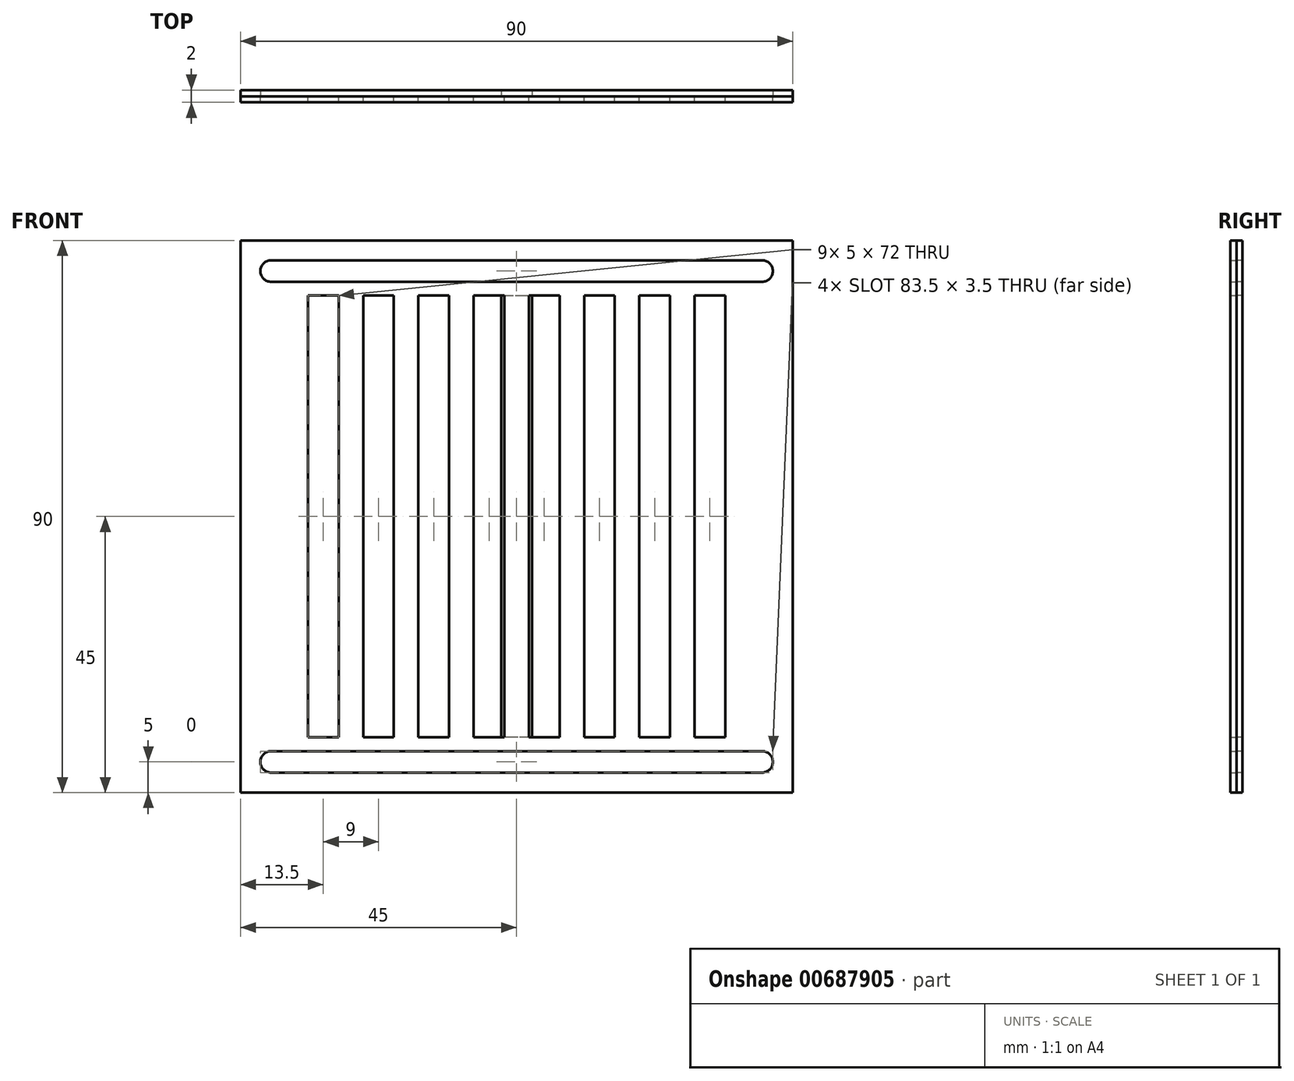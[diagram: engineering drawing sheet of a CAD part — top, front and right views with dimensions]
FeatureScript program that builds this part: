
annotation { "Feature Type Name" : "Feature", "Feature Type Description" : "" }
export const myFeature = defineFeature(function(context is Context, id is Id, definition is map)
    precondition{}
    {
        {
            var Q0;
            Q0=qCreatedBy(makeId("Front.planeOp"),FACE);
            var sketch = newSketch(context, id + "F0", { "sketchPlane" : qUnion([Q0])});
            skLineSegment(sketch, "E0.bottom", {"start": v(-45, 45) * mm, "end": v(45, 45) * mm});
            skLineSegment(sketch, "E0.top", {"start": v(-45, -45) * mm, "end": v(45, -45) * mm});
            skLineSegment(sketch, "E0.left", {"start": v(-45, 45) * mm, "end": v(-45, -45) * mm});
            skLineSegment(sketch, "E0.right", {"start": v(45, 45) * mm, "end": v(45, -45) * mm});
            skPoint(sketch, "E0.middle", {"position": v(0, 0) * mm});
            skLineSegment(sketch, "E1", {"start": v(0, 41.75) * mm, "end": v(40, 41.75) * mm});
            skLineSegment(sketch, "E2", {"start": v(0, 38.25) * mm, "end": v(40, 38.25) * mm});
            skArc(sketch, "E3", {"start": v(40, 41.75) * mm, "mid": v(41.75, 40) * mm, "end": v(40, 38.25) * mm});
            skLineSegment(sketch, "E4.top", {"start": v(2, 36) * mm, "end": v(7, 36) * mm});
            skLineSegment(sketch, "E4.left", {"start": v(2, 0) * mm, "end": v(2, 36) * mm});
            skLineSegment(sketch, "E4.right", {"start": v(7, 0) * mm, "end": v(7, 36) * mm});
            skLineSegment(sketch, "E5.1.0.0", {"start": v(11, 0) * mm, "end": v(11, 36) * mm});
            skLineSegment(sketch, "E5.1.0.1", {"start": v(11, 36) * mm, "end": v(16, 36) * mm});
            skLineSegment(sketch, "E5.1.0.2", {"start": v(16, 0) * mm, "end": v(16, 36) * mm});
            skLineSegment(sketch, "E5.2.0.0", {"start": v(20, 0) * mm, "end": v(20, 36) * mm});
            skLineSegment(sketch, "E5.2.0.1", {"start": v(20, 36) * mm, "end": v(25, 36) * mm});
            skLineSegment(sketch, "E5.2.0.2", {"start": v(25, 0) * mm, "end": v(25, 36) * mm});
            skLineSegment(sketch, "E5.3.0.0", {"start": v(29, 0) * mm, "end": v(29, 36) * mm});
            skLineSegment(sketch, "E5.3.0.1", {"start": v(29, 36) * mm, "end": v(34, 36) * mm});
            skLineSegment(sketch, "E5.3.0.2", {"start": v(34, 0) * mm, "end": v(34, 36) * mm});
            skLineSegment(sketch, "E5.direction1", {"start": v(2, 0) * mm, "end": v(12, 0) * mm, "construction": true});
            skLineSegment(sketch, "E6.MirrorCS", {"start": v(-25, 0) * mm, "end": v(-25, 36) * mm});
            skLineSegment(sketch, "E7.MirrorCS", {"start": v(-20, 36) * mm, "end": v(-25, 36) * mm});
            skLineSegment(sketch, "E8.MirrorCS", {"start": v(-20, 0) * mm, "end": v(-20, 36) * mm});
            skLineSegment(sketch, "E9.MirrorCS", {"start": v(-2, 0) * mm, "end": v(-12, 0) * mm, "construction": true});
            skLineSegment(sketch, "E10.MirrorCS", {"start": v(-29, 36) * mm, "end": v(-34, 36) * mm});
            skLineSegment(sketch, "E11.MirrorCS", {"start": v(-29, 0) * mm, "end": v(-29, 36) * mm});
            skLineSegment(sketch, "E12.MirrorCS", {"start": v(-16, 0) * mm, "end": v(-16, 36) * mm});
            skLineSegment(sketch, "E13.MirrorCS", {"start": v(-11, 36) * mm, "end": v(-16, 36) * mm});
            skLineSegment(sketch, "E14.MirrorCS", {"start": v(-34, 0) * mm, "end": v(-34, 36) * mm});
            skLineSegment(sketch, "E15.MirrorCS", {"start": v(0, 41.75) * mm, "end": v(-40, 41.75) * mm});
            skLineSegment(sketch, "E16.MirrorCS", {"start": v(-2, 36) * mm, "end": v(-7, 36) * mm});
            skLineSegment(sketch, "E17.MirrorCS", {"start": v(-2, 0) * mm, "end": v(-2, 36) * mm});
            skArc(sketch, "E18.MirrorCS", {"start": v(-40, 41.75) * mm, "mid": v(-41.75, 40) * mm, "end": v(-40, 38.25) * mm});
            skLineSegment(sketch, "E19.MirrorCS", {"start": v(-7, 0) * mm, "end": v(-7, 36) * mm});
            skLineSegment(sketch, "E20.MirrorCS", {"start": v(-11, 0) * mm, "end": v(-11, 36) * mm});
            skLineSegment(sketch, "E21.MirrorCS", {"start": v(0, 38.25) * mm, "end": v(-40, 38.25) * mm});
            skArc(sketch, "E22.MirrorCS", {"start": v(40, -41.75) * mm, "mid": v(41.75, -40) * mm, "end": v(40, -38.25) * mm});
            skArc(sketch, "E23.MirrorCS", {"start": v(-40, -41.75) * mm, "mid": v(-41.75, -40) * mm, "end": v(-40, -38.25) * mm});
            skLineSegment(sketch, "E24.MirrorCS", {"start": v(-7, 0) * mm, "end": v(-7, -36) * mm});
            skLineSegment(sketch, "E25.MirrorCS", {"start": v(25, 0) * mm, "end": v(25, -36) * mm});
            skLineSegment(sketch, "E26.MirrorCS", {"start": v(29, 0) * mm, "end": v(29, -36) * mm});
            skLineSegment(sketch, "E27.MirrorCS", {"start": v(-11, 0) * mm, "end": v(-11, -36) * mm});
            skLineSegment(sketch, "E28.MirrorCS", {"start": v(34, 0) * mm, "end": v(34, -36) * mm});
            skLineSegment(sketch, "E29.MirrorCS", {"start": v(0, -41.75) * mm, "end": v(-40, -41.75) * mm});
            skLineSegment(sketch, "E30.MirrorCS", {"start": v(-25, 0) * mm, "end": v(-25, -36) * mm});
            skLineSegment(sketch, "E31.MirrorCS", {"start": v(-2, 0) * mm, "end": v(-2, -36) * mm});
            skLineSegment(sketch, "E32.MirrorCS", {"start": v(-20, 0) * mm, "end": v(-20, -36) * mm});
            skLineSegment(sketch, "E33.MirrorCS", {"start": v(-29, 0) * mm, "end": v(-29, -36) * mm});
            skLineSegment(sketch, "E34.MirrorCS", {"start": v(-11, -36) * mm, "end": v(-16, -36) * mm});
            skLineSegment(sketch, "E35.MirrorCS", {"start": v(16, 0) * mm, "end": v(16, -36) * mm});
            skLineSegment(sketch, "E36.MirrorCS", {"start": v(11, -36) * mm, "end": v(16, -36) * mm});
            skLineSegment(sketch, "E37.MirrorCS", {"start": v(11, 0) * mm, "end": v(11, -36) * mm});
            skLineSegment(sketch, "E38.MirrorCS", {"start": v(7, 0) * mm, "end": v(7, -36) * mm});
            skLineSegment(sketch, "E39.MirrorCS", {"start": v(2, 0) * mm, "end": v(2, -36) * mm});
            skLineSegment(sketch, "E40.MirrorCS", {"start": v(2, -36) * mm, "end": v(7, -36) * mm});
            skLineSegment(sketch, "E41.MirrorCS", {"start": v(20, -36) * mm, "end": v(25, -36) * mm});
            skLineSegment(sketch, "E42.MirrorCS", {"start": v(29, -36) * mm, "end": v(34, -36) * mm});
            skLineSegment(sketch, "E43.MirrorCS", {"start": v(20, 0) * mm, "end": v(20, -36) * mm});
            skLineSegment(sketch, "E44.MirrorCS", {"start": v(0, -38.25) * mm, "end": v(-40, -38.25) * mm});
            skLineSegment(sketch, "E45.MirrorCS", {"start": v(-34, 0) * mm, "end": v(-34, -36) * mm});
            skLineSegment(sketch, "E46.MirrorCS", {"start": v(-16, 0) * mm, "end": v(-16, -36) * mm});
            skLineSegment(sketch, "E47.MirrorCS", {"start": v(-29, -36) * mm, "end": v(-34, -36) * mm});
            skLineSegment(sketch, "E48.MirrorCS", {"start": v(-20, -36) * mm, "end": v(-25, -36) * mm});
            skLineSegment(sketch, "E49.MirrorCS", {"start": v(-2, -36) * mm, "end": v(-7, -36) * mm});
            skLineSegment(sketch, "E50.MirrorCS", {"start": v(0, -41.75) * mm, "end": v(40, -41.75) * mm});
            skLineSegment(sketch, "E51.MirrorCS", {"start": v(0, -38.25) * mm, "end": v(40, -38.25) * mm});
            skSolve(sketch);
        }
        {
            var Q0;
            Q0=makeQuery(id+"F0.imprint","IMPRINT",FACE,{"disambiguationData":[TD([[makeQuery(id+"F0.imprint","IMPRINT",EDGE,{"derivedFrom":sQuery(id+"F0.wireOp",EDGE,"E0.bottom")}),-1.0]])]});
            extrude(context, id + "F1", {"entities" : qUnion([Q0]), "depth" : 1 * mm, "offsetDistance" : 25 * mm});
        }
        {
            var Q0;
            Q0=makeQuery(id+"F1.opExtrude","CAP_FACE",FACE,{"disambiguationData":[OSD([sQuery(id+"F0.wireOp",EDGE,"E0.bottom"),sQuery(id+"F0.wireOp",EDGE,"E0.top"),sQuery(id+"F0.wireOp",EDGE,"E0.left"),sQuery(id+"F0.wireOp",EDGE,"E0.right"),sQuery(id+"F0.wireOp",EDGE,"E1"),sQuery(id+"F0.wireOp",EDGE,"E2"),sQuery(id+"F0.wireOp",EDGE,"E3"),sQuery(id+"F0.wireOp",EDGE,"E4.top"),sQuery(id+"F0.wireOp",EDGE,"E4.left"),sQuery(id+"F0.wireOp",EDGE,"E4.right"),sQuery(id+"F0.wireOp",EDGE,"E5.1.0.0"),sQuery(id+"F0.wireOp",EDGE,"E5.1.0.1"),sQuery(id+"F0.wireOp",EDGE,"E5.1.0.2"),sQuery(id+"F0.wireOp",EDGE,"E5.2.0.0"),sQuery(id+"F0.wireOp",EDGE,"E5.2.0.1"),sQuery(id+"F0.wireOp",EDGE,"E5.2.0.2"),sQuery(id+"F0.wireOp",EDGE,"E5.3.0.0"),sQuery(id+"F0.wireOp",EDGE,"E5.3.0.1"),sQuery(id+"F0.wireOp",EDGE,"E5.3.0.2"),sQuery(id+"F0.wireOp",EDGE,"E6.MirrorCS"),sQuery(id+"F0.wireOp",EDGE,"E7.MirrorCS"),sQuery(id+"F0.wireOp",EDGE,"E8.MirrorCS"),sQuery(id+"F0.wireOp",EDGE,"E10.MirrorCS"),sQuery(id+"F0.wireOp",EDGE,"E11.MirrorCS"),sQuery(id+"F0.wireOp",EDGE,"E12.MirrorCS"),sQuery(id+"F0.wireOp",EDGE,"E13.MirrorCS"),sQuery(id+"F0.wireOp",EDGE,"E14.MirrorCS"),sQuery(id+"F0.wireOp",EDGE,"E15.MirrorCS"),sQuery(id+"F0.wireOp",EDGE,"E16.MirrorCS"),sQuery(id+"F0.wireOp",EDGE,"E17.MirrorCS"),sQuery(id+"F0.wireOp",EDGE,"E18.MirrorCS"),sQuery(id+"F0.wireOp",EDGE,"E19.MirrorCS"),sQuery(id+"F0.wireOp",EDGE,"E20.MirrorCS"),sQuery(id+"F0.wireOp",EDGE,"E21.MirrorCS"),sQuery(id+"F0.wireOp",EDGE,"E22.MirrorCS"),sQuery(id+"F0.wireOp",EDGE,"E23.MirrorCS"),sQuery(id+"F0.wireOp",EDGE,"E24.MirrorCS"),sQuery(id+"F0.wireOp",EDGE,"E25.MirrorCS"),sQuery(id+"F0.wireOp",EDGE,"E26.MirrorCS"),sQuery(id+"F0.wireOp",EDGE,"E27.MirrorCS"),sQuery(id+"F0.wireOp",EDGE,"E28.MirrorCS"),sQuery(id+"F0.wireOp",EDGE,"E29.MirrorCS"),sQuery(id+"F0.wireOp",EDGE,"E30.MirrorCS"),sQuery(id+"F0.wireOp",EDGE,"E31.MirrorCS"),sQuery(id+"F0.wireOp",EDGE,"E32.MirrorCS"),sQuery(id+"F0.wireOp",EDGE,"E33.MirrorCS"),sQuery(id+"F0.wireOp",EDGE,"E34.MirrorCS"),sQuery(id+"F0.wireOp",EDGE,"E35.MirrorCS"),sQuery(id+"F0.wireOp",EDGE,"E36.MirrorCS"),sQuery(id+"F0.wireOp",EDGE,"E37.MirrorCS"),sQuery(id+"F0.wireOp",EDGE,"E38.MirrorCS"),sQuery(id+"F0.wireOp",EDGE,"E39.MirrorCS"),sQuery(id+"F0.wireOp",EDGE,"E40.MirrorCS"),sQuery(id+"F0.wireOp",EDGE,"E41.MirrorCS"),sQuery(id+"F0.wireOp",EDGE,"E42.MirrorCS"),sQuery(id+"F0.wireOp",EDGE,"E43.MirrorCS"),sQuery(id+"F0.wireOp",EDGE,"E44.MirrorCS"),sQuery(id+"F0.wireOp",EDGE,"E45.MirrorCS"),sQuery(id+"F0.wireOp",EDGE,"E46.MirrorCS"),sQuery(id+"F0.wireOp",EDGE,"E47.MirrorCS"),sQuery(id+"F0.wireOp",EDGE,"E48.MirrorCS"),sQuery(id+"F0.wireOp",EDGE,"E49.MirrorCS"),sQuery(id+"F0.wireOp",EDGE,"E50.MirrorCS"),sQuery(id+"F0.wireOp",EDGE,"E51.MirrorCS")])],"isStart":true});
            var sketch = newSketch(context, id + "F2", { "sketchPlane" : qUnion([Q0])});
            skLineSegment(sketch, "E52.bottom", {"start": v(-45, 45) * mm, "end": v(45, 45) * mm});
            skLineSegment(sketch, "E52.top", {"start": v(-45, -45) * mm, "end": v(45, -45) * mm});
            skLineSegment(sketch, "E52.left", {"start": v(-45, 45) * mm, "end": v(-45, -45) * mm});
            skLineSegment(sketch, "E52.right", {"start": v(45, 45) * mm, "end": v(45, -45) * mm});
            skPoint(sketch, "E52.middle", {"position": v(0, 0) * mm});
            skLineSegment(sketch, "E53.bottom", {"start": v(2.5, 36) * mm, "end": v(-2.5, 36) * mm});
            skLineSegment(sketch, "E53.top", {"start": v(2.5, -36) * mm, "end": v(-2.5, -36) * mm});
            skLineSegment(sketch, "E53.left", {"start": v(2.5, 36) * mm, "end": v(2.5, -36) * mm});
            skLineSegment(sketch, "E53.right", {"start": v(-2.5, 36) * mm, "end": v(-2.5, -36) * mm});
            skLineSegment(sketch, "E54", {"start": v(0, 41.75) * mm, "end": v(0, -45) * mm, "construction": true});
            skPoint(sketch, "E55", {"position": v(0, 36) * mm});
            skSolve(sketch);
        }
        {
            var Q0;
            Q0=makeQuery(id+"F2.imprint","IMPRINT",FACE,{"disambiguationData":[TD([[makeQuery(id+"F2.imprint","IMPRINT",EDGE,{"derivedFrom":makeQuery(id+"F1.opExtrude","CAP_EDGE",EDGE,{"disambiguationData":[OSD([sQuery(id+"F0.wireOp",EDGE,"E4.top")])],"isStart":true})}),1.0]])]});
            var Q1;
            Q1=makeQuery(id+"F2.imprint","IMPRINT",FACE,{"disambiguationData":[TD([[makeQuery(id+"F2.imprint","IMPRINT",EDGE,{"derivedFrom":makeQuery(id+"F1.opExtrude","CAP_EDGE",EDGE,{"disambiguationData":[OSD([sQuery(id+"F0.wireOp",EDGE,"E5.1.0.1")])],"isStart":true})}),1.0]])]});
            var Q2;
            Q2=makeQuery(id+"F2.imprint","IMPRINT",FACE,{"disambiguationData":[TD([[makeQuery(id+"F2.imprint","IMPRINT",EDGE,{"derivedFrom":makeQuery(id+"F1.opExtrude","CAP_EDGE",EDGE,{"disambiguationData":[OSD([sQuery(id+"F0.wireOp",EDGE,"E5.2.0.1")])],"isStart":true})}),1.0]])]});
            var Q3;
            Q3=makeQuery(id+"F2.imprint","IMPRINT",FACE,{"disambiguationData":[TD([[makeQuery(id+"F2.imprint","IMPRINT",EDGE,{"derivedFrom":makeQuery(id+"F1.opExtrude","CAP_EDGE",EDGE,{"disambiguationData":[OSD([sQuery(id+"F0.wireOp",EDGE,"E5.3.0.1")])],"isStart":true})}),1.0]])]});
            var Q4;
            Q4=makeQuery(id+"F2.imprint","IMPRINT",FACE,{"disambiguationData":[TD([[makeQuery(id+"F2.imprint","IMPRINT",EDGE,{"derivedFrom":makeQuery(id+"F1.opExtrude","CAP_EDGE",EDGE,{"disambiguationData":[OSD([sQuery(id+"F0.wireOp",EDGE,"E7.MirrorCS")])],"isStart":true})}),-1.0]])]});
            var Q5;
            Q5=makeQuery(id+"F2.imprint","IMPRINT",FACE,{"disambiguationData":[TD([[makeQuery(id+"F2.imprint","IMPRINT",EDGE,{"derivedFrom":makeQuery(id+"F1.opExtrude","CAP_EDGE",EDGE,{"disambiguationData":[OSD([sQuery(id+"F0.wireOp",EDGE,"E10.MirrorCS")])],"isStart":true})}),-1.0]])]});
            var Q6;
            Q6=makeQuery(id+"F2.imprint","IMPRINT",FACE,{"disambiguationData":[TD([[makeQuery(id+"F2.imprint","IMPRINT",EDGE,{"derivedFrom":makeQuery(id+"F1.opExtrude","CAP_EDGE",EDGE,{"disambiguationData":[OSD([sQuery(id+"F0.wireOp",EDGE,"E13.MirrorCS")])],"isStart":true})}),-1.0]])]});
            var Q7;
            Q7=makeQuery(id+"F2.imprint","IMPRINT",FACE,{"disambiguationData":[TD([[makeQuery(id+"F2.imprint","IMPRINT",EDGE,{"derivedFrom":makeQuery(id+"F1.opExtrude","CAP_EDGE",EDGE,{"disambiguationData":[OSD([sQuery(id+"F0.wireOp",EDGE,"E16.MirrorCS")])],"isStart":true})}),-1.0]])]});
            var Q8;
            Q8=makeQuery(id+"F2.imprint","IMPRINT",FACE,{"disambiguationData":[TD([[makeQuery(id+"F2.imprint","IMPRINT",EDGE,{"derivedFrom":sQuery(id+"F2.wireOp",EDGE,"E52.bottom")}),1.0]])]});
            extrude(context, id + "F3", {"entities" : qUnion([Q0, Q1, Q2, Q3, Q4, Q5, Q6, Q7, Q8]), "depth" : 1 * mm, "offsetDistance" : 25 * mm});
        }
    });
